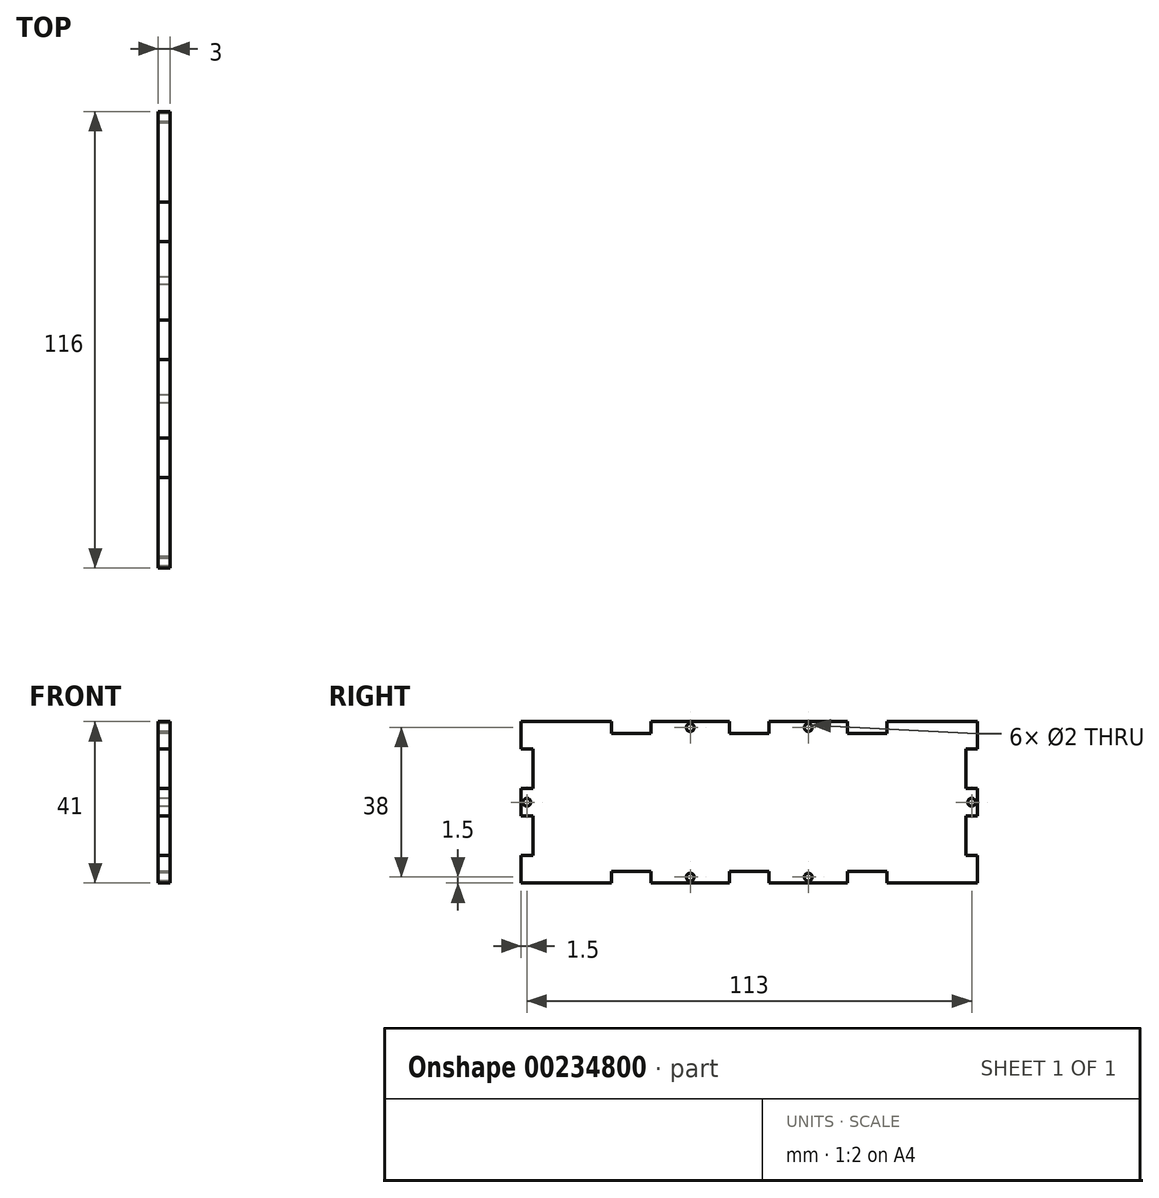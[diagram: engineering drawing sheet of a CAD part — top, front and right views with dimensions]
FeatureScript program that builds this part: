
annotation { "Feature Type Name" : "Feature", "Feature Type Description" : "" }
export const myFeature = defineFeature(function(context is Context, id is Id, definition is map)
    precondition{}
    {
        {
            var Q0;
            Q0=qCreatedBy(makeId("Right.planeOp"),FACE);
            var sketch = newSketch(context, id + "F0", { "sketchPlane" : qUnion([Q0])});
            skLineSegment(sketch, "E0.bottom", {"start": v(0, 0) * mm, "end": v(58, 0) * mm});
            skLineSegment(sketch, "E0.top", {"start": v(5, 20.5) * mm, "end": v(25, 20.5) * mm});
            skLineSegment(sketch, "E0.left", {"start": v(0, 0) * mm, "end": v(0, 17.5) * mm});
            skLineSegment(sketch, "E0.right", {"start": v(58, 0) * mm, "end": v(58, 3.5) * mm});
            skLineSegment(sketch, "E1", {"start": v(35, 20.5) * mm, "end": v(35, 17.5) * mm});
            skLineSegment(sketch, "E2", {"start": v(35, 17.5) * mm, "end": v(25, 17.5) * mm});
            skLineSegment(sketch, "E3", {"start": v(25, 17.5) * mm, "end": v(25, 20.5) * mm});
            skLineSegment(sketch, "E4", {"start": v(5, 20.5) * mm, "end": v(5, 17.5) * mm});
            skLineSegment(sketch, "E5", {"start": v(5, 17.5) * mm, "end": v(0, 17.5) * mm});
            skLineSegment(sketch, "E6", {"start": v(58, 13.5) * mm, "end": v(55, 13.5) * mm});
            skLineSegment(sketch, "E7", {"start": v(55, 13.5) * mm, "end": v(55, 3.5) * mm});
            skLineSegment(sketch, "E8", {"start": v(55, 3.5) * mm, "end": v(58, 3.5) * mm});
            skLineSegment(sketch, "E9.trimOffspring", {"start": v(35, 20.5) * mm, "end": v(58, 20.5) * mm});
            skLineSegment(sketch, "E10.trimOffspring", {"start": v(58, 13.5) * mm, "end": v(58, 20.5) * mm});
            skCircle(sketch, "E11", {"center": v(15, 19) * mm, "radius": 1 * mm});
            skLineSegment(sketch, "E12.MirrorCS", {"start": v(55, -3.5) * mm, "end": v(58, -3.5) * mm});
            skLineSegment(sketch, "E13.MirrorCS", {"start": v(58, -13.5) * mm, "end": v(58, -20.5) * mm});
            skLineSegment(sketch, "E14.MirrorCS", {"start": v(58, -13.5) * mm, "end": v(55, -13.5) * mm});
            skLineSegment(sketch, "E15.MirrorCS", {"start": v(5, -20.5) * mm, "end": v(5, -17.5) * mm});
            skLineSegment(sketch, "E16.MirrorCS", {"start": v(55, -13.5) * mm, "end": v(55, -3.5) * mm});
            skCircle(sketch, "E17.MirrorC", {"center": v(15, -19) * mm, "radius": 1 * mm});
            skLineSegment(sketch, "E18.MirrorCS", {"start": v(5, -20.5) * mm, "end": v(25, -20.5) * mm});
            skLineSegment(sketch, "E19.MirrorCS", {"start": v(35, -17.5) * mm, "end": v(25, -17.5) * mm});
            skLineSegment(sketch, "E20.MirrorCS", {"start": v(35, -20.5) * mm, "end": v(35, -17.5) * mm});
            skLineSegment(sketch, "E21.MirrorCS", {"start": v(25, -17.5) * mm, "end": v(25, -20.5) * mm});
            skLineSegment(sketch, "E22.MirrorCS", {"start": v(35, -20.5) * mm, "end": v(58, -20.5) * mm});
            skLineSegment(sketch, "E23.MirrorCS", {"start": v(0, 0) * mm, "end": v(0, -17.5) * mm});
            skLineSegment(sketch, "E24.MirrorCS", {"start": v(58, 0) * mm, "end": v(58, -3.5) * mm});
            skLineSegment(sketch, "E25.MirrorCS", {"start": v(5, -17.5) * mm, "end": v(0, -17.5) * mm});
            skCircle(sketch, "E26", {"center": v(56.5, 0) * mm, "radius": 1 * mm});
            skLineSegment(sketch, "E27.MirrorCS", {"start": v(-58, -13.5) * mm, "end": v(-58, -20.5) * mm});
            skLineSegment(sketch, "E28.MirrorCS", {"start": v(-5, -20.5) * mm, "end": v(-5, -17.5) * mm});
            skCircle(sketch, "E29.MirrorC", {"center": v(-56.5, 0) * mm, "radius": 1 * mm});
            skCircle(sketch, "E30.MirrorC", {"center": v(-15, -19) * mm, "radius": 1 * mm});
            skLineSegment(sketch, "E31.MirrorCS", {"start": v(-35, -17.5) * mm, "end": v(-25, -17.5) * mm});
            skLineSegment(sketch, "E32.MirrorCS", {"start": v(-35, -20.5) * mm, "end": v(-35, -17.5) * mm});
            skLineSegment(sketch, "E33.MirrorCS", {"start": v(-35, -20.5) * mm, "end": v(-58, -20.5) * mm});
            skLineSegment(sketch, "E34.MirrorCS", {"start": v(-58, 0) * mm, "end": v(-58, -3.5) * mm});
            skLineSegment(sketch, "E35.MirrorCS", {"start": v(-35, 20.5) * mm, "end": v(-58, 20.5) * mm});
            skLineSegment(sketch, "E36.MirrorCS", {"start": v(-55, 3.5) * mm, "end": v(-58, 3.5) * mm});
            skLineSegment(sketch, "E37.MirrorCS", {"start": v(-55, 13.5) * mm, "end": v(-55, 3.5) * mm});
            skLineSegment(sketch, "E38.MirrorCS", {"start": v(-58, 13.5) * mm, "end": v(-55, 13.5) * mm});
            skLineSegment(sketch, "E39.MirrorCS", {"start": v(-5, 17.5) * mm, "end": v(0, 17.5) * mm});
            skLineSegment(sketch, "E40.MirrorCS", {"start": v(-5, 20.5) * mm, "end": v(-5, 17.5) * mm});
            skLineSegment(sketch, "E41.MirrorCS", {"start": v(-25, 17.5) * mm, "end": v(-25, 20.5) * mm});
            skLineSegment(sketch, "E42.MirrorCS", {"start": v(-35, 17.5) * mm, "end": v(-25, 17.5) * mm});
            skLineSegment(sketch, "E43.MirrorCS", {"start": v(-35, 20.5) * mm, "end": v(-35, 17.5) * mm});
            skLineSegment(sketch, "E44.MirrorCS", {"start": v(-58, 0) * mm, "end": v(-58, 3.5) * mm});
            skLineSegment(sketch, "E45.MirrorCS", {"start": v(-25, -17.5) * mm, "end": v(-25, -20.5) * mm});
            skLineSegment(sketch, "E46.MirrorCS", {"start": v(-58, 13.5) * mm, "end": v(-58, 20.5) * mm});
            skLineSegment(sketch, "E47.MirrorCS", {"start": v(-5, 20.5) * mm, "end": v(-25, 20.5) * mm});
            skLineSegment(sketch, "E48.MirrorCS", {"start": v(-55, -13.5) * mm, "end": v(-55, -3.5) * mm});
            skLineSegment(sketch, "E49.MirrorCS", {"start": v(0, 0) * mm, "end": v(-58, 0) * mm});
            skLineSegment(sketch, "E50.MirrorCS", {"start": v(-58, -13.5) * mm, "end": v(-55, -13.5) * mm});
            skLineSegment(sketch, "E51.MirrorCS", {"start": v(-5, -17.5) * mm, "end": v(0, -17.5) * mm});
            skLineSegment(sketch, "E52.MirrorCS", {"start": v(-55, -3.5) * mm, "end": v(-58, -3.5) * mm});
            skLineSegment(sketch, "E53.MirrorCS", {"start": v(-5, -20.5) * mm, "end": v(-25, -20.5) * mm});
            skCircle(sketch, "E54.MirrorC", {"center": v(-15, 19) * mm, "radius": 1 * mm});
            skSolve(sketch);
        }
        {
            var Q0;
            Q0 = qSketchRegion(id + "F0", true);
            extrude(context, id + "F1", {"entities" : qUnion([Q0]), "endBound" : BoundingType.SYMMETRIC, "depth" : 3 * mm});
        }
    });
